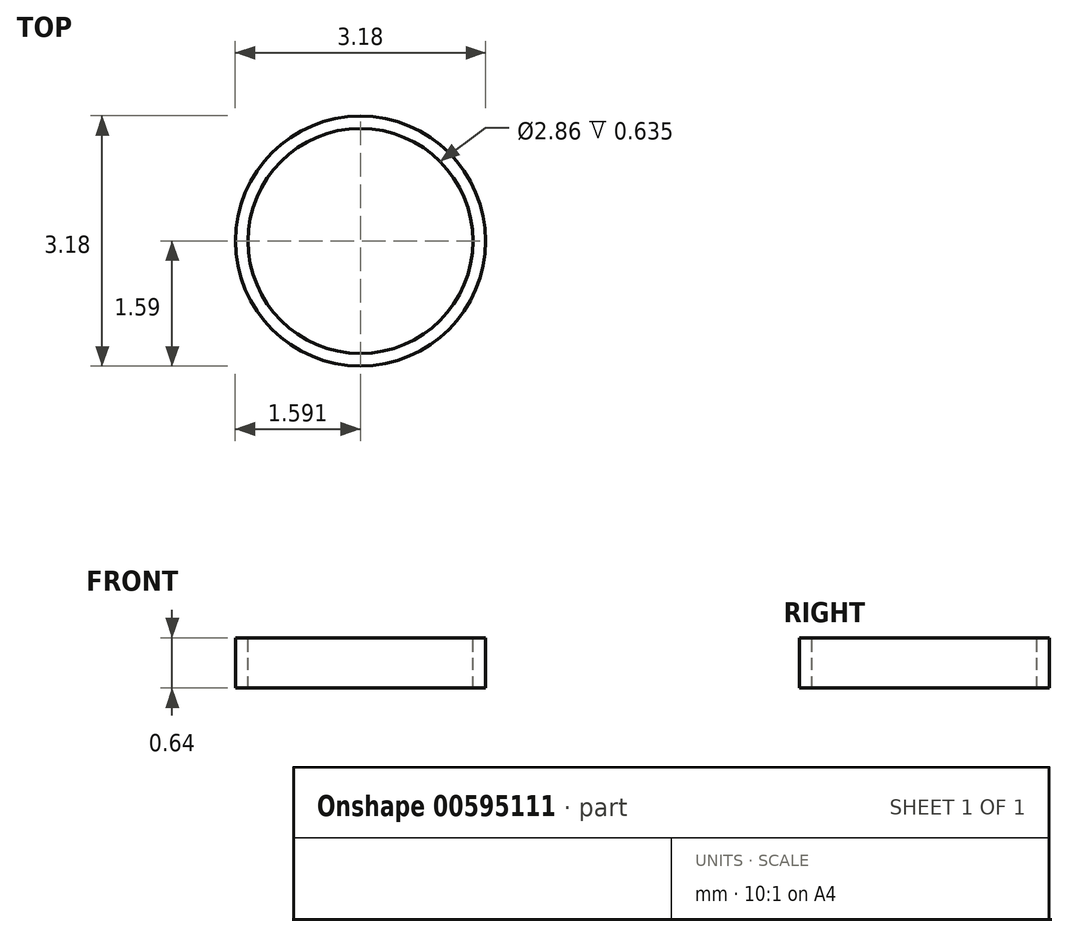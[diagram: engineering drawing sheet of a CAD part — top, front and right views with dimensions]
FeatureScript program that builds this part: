
annotation { "Feature Type Name" : "Feature", "Feature Type Description" : "" }
export const myFeature = defineFeature(function(context is Context, id is Id, definition is map)
    precondition{}
    {
        {
            var Q0;
            Q0=qCreatedBy(makeId("Top.planeOp"),FACE);
            var sketch = newSketch(context, id + "F0", { "sketchPlane" : qUnion([Q0])});
            skCircle(sketch, "E0", {"center": v(-52.58, 54.56) * mm, "radius": 3.18 * mm});
            skSolve(sketch);
        }
        {
            var Q0;
            Q0=makeQuery(id+"F0.imprint","IMPRINT",FACE,{"disambiguationData":[TD([[makeQuery(id+"F0.imprint","IMPRINT",EDGE,{"derivedFrom":sQuery(id+"F0.wireOp",EDGE,"E0")}),1.0]])]});
            extrude(context, id + "F1", {"entities" : qUnion([Q0]), "depth" : 1.27 * mm, "offsetDistance" : 25.4 * mm});
        }
        {
            var Q0;
            Q0=makeQuery(id+"F1.opExtrude","CAP_FACE",FACE,{"disambiguationData":[OSD([sQuery(id+"F0.wireOp",EDGE,"E0")])],"isStart":false});
            var sketch = newSketch(context, id + "F2", { "sketchPlane" : qUnion([Q0])});
            skCircle(sketch, "E1", {"center": v(-52.58, 54.56) * mm, "radius": 2.54 * mm});
            skSolve(sketch);
        }
        {
            var Q0;
            Q0=sQuery(id+"F2.wireOp",VERTEX,"E1.center");
            var Q1;
            Q1=makeQuery(id+"F1.opExtrude","SWEPT_BODY",BODY,{"disambiguationData":[OSD([sQuery(id+"F0.wireOp",EDGE,"E0")])]});
            hole(context, id + "F3", {"style" : HoleStyle.SIMPLE, "endStyle" : HoleEndStyle.THROUGH, "holeDiameter" : 5.7 * mm, "majorDiameter" : 6.35 * mm, "isTappedThrough" : true, "tappedDepth" : 12.7 * mm, "tapClearance" : 3, "locations" : qUnion([Q0]), "scope" : qUnion([Q1])});
        }
        {
            var Q0;
            Q0=makeQuery(id+"F1.opExtrude","SWEPT_BODY",BODY,{"disambiguationData":[OSD([sQuery(id+"F0.wireOp",EDGE,"E0")])]});
            var Q1;
            Q1=qCreatedBy(makeId("Origin.pointOp"),VERTEX);
            transform(context, id + "F4", {"entities" : qUnion([Q0]), "transformType" : TransformType.SCALE_UNIFORMLY, "scale" : .5, "scalePoint" : qUnion([Q1]), "makeCopy" : false});
        }
    });
